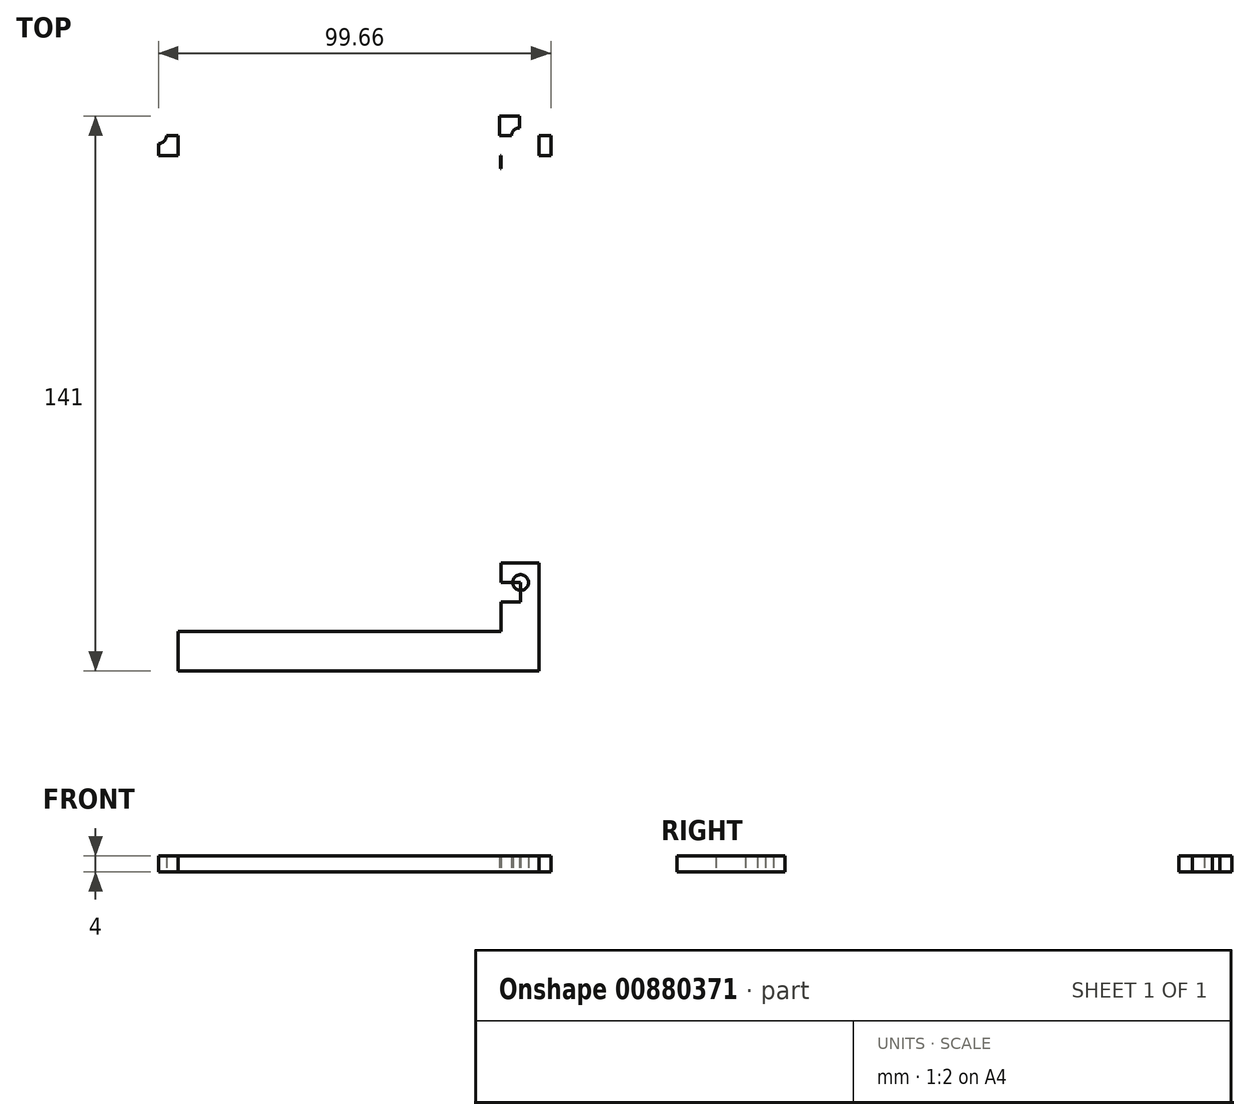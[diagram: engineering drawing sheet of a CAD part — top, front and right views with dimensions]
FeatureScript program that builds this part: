
annotation { "Feature Type Name" : "Feature", "Feature Type Description" : "" }
export const myFeature = defineFeature(function(context is Context, id is Id, definition is map)
    precondition{}
    {
        {
            var Q0;
            Q0=qCreatedBy(makeId("Top.planeOp"),FACE);
            var sketch = newSketch(context, id + "F0", { "sketchPlane" : qUnion([Q0])});
            skLineSegment(sketch, "E0.bottom", {"start": v(-139.68, -1.26) * mm, "end": v(-129.68, -1.26) * mm});
            skLineSegment(sketch, "E0.top", {"start": v(-139.68, -11.26) * mm, "end": v(-129.68, -11.26) * mm});
            skLineSegment(sketch, "E0.left", {"start": v(-139.68, -1.26) * mm, "end": v(-139.68, -11.26) * mm});
            skLineSegment(sketch, "E0.right", {"start": v(-129.68, -1.26) * mm, "end": v(-129.68, -11.26) * mm});
            skLineSegment(sketch, "E1.left", {"start": v(-129.68, -11.26) * mm, "end": v(-129.68, -114.76) * mm});
            skLineSegment(sketch, "E2.bottom", {"start": v(-124.68, -124.58) * mm, "end": v(-98.18, -124.58) * mm});
            skLineSegment(sketch, "E2.top", {"start": v(-124.68, -88.58) * mm, "end": v(-98.18, -88.58) * mm});
            skLineSegment(sketch, "E2.left", {"start": v(-124.68, -124.58) * mm, "end": v(-124.68, -88.58) * mm});
            skLineSegment(sketch, "E2.right", {"start": v(-98.18, -124.58) * mm, "end": v(-98.18, -88.58) * mm});
            skLineSegment(sketch, "E3.bottom", {"start": v(-129.68, -114.76) * mm, "end": v(-139.34, -114.76) * mm});
            skLineSegment(sketch, "E3.top", {"start": v(-129.68, -124.76) * mm, "end": v(-139.34, -124.76) * mm});
            skLineSegment(sketch, "E3.left", {"start": v(-129.68, -114.76) * mm, "end": v(-129.68, -124.76) * mm});
            skLineSegment(sketch, "E3.right", {"start": v(-139.34, -114.76) * mm, "end": v(-139.34, -124.76) * mm});
            skLineSegment(sketch, "E4", {"start": v(-129.68, -11.26) * mm, "end": v(-126.34, -11.26) * mm});
            skLineSegment(sketch, "E5.bottom", {"start": v(-129.68, -11.26) * mm, "end": v(-126.88, -11.26) * mm});
            skLineSegment(sketch, "E5.left", {"start": v(-129.68, -11.26) * mm, "end": v(-129.68, -14.06) * mm});
            skLineSegment(sketch, "E6.left", {"start": v(-129.68, -114.76) * mm, "end": v(-129.68, -111.76) * mm});
            skLineSegment(sketch, "E7.bottom", {"start": v(-98.18, -88.58) * mm, "end": v(-99.88, -88.58) * mm});
            skLineSegment(sketch, "E7.top", {"start": v(-98.18, -90.28) * mm, "end": v(-99.88, -90.28) * mm});
            skLineSegment(sketch, "E7.left", {"start": v(-98.18, -88.58) * mm, "end": v(-98.18, -90.28) * mm});
            skLineSegment(sketch, "E7.right", {"start": v(-99.88, -88.58) * mm, "end": v(-99.88, -90.28) * mm});
            skLineSegment(sketch, "E8.bottom", {"start": v(-124.68, -88.58) * mm, "end": v(-122.98, -88.58) * mm});
            skLineSegment(sketch, "E8.top", {"start": v(-124.68, -90.28) * mm, "end": v(-122.98, -90.28) * mm});
            skLineSegment(sketch, "E8.left", {"start": v(-124.68, -88.58) * mm, "end": v(-124.68, -90.28) * mm});
            skLineSegment(sketch, "E8.right", {"start": v(-122.98, -88.58) * mm, "end": v(-122.98, -90.28) * mm});
            skCircle(sketch, "E9", {"center": v(-122.98, -90.28) * mm, "radius": 1.2 * mm});
            skCircle(sketch, "E10", {"center": v(-99.88, -90.28) * mm, "radius": 1.2 * mm});
            skLineSegment(sketch, "E11.bottom", {"start": v(-139.34, -124.76) * mm, "end": v(-134.34, -124.76) * mm});
            skLineSegment(sketch, "E11.top", {"start": v(-139.34, -119.76) * mm, "end": v(-134.34, -119.76) * mm});
            skLineSegment(sketch, "E11.left", {"start": v(-139.34, -124.76) * mm, "end": v(-139.34, -119.76) * mm});
            skLineSegment(sketch, "E11.right", {"start": v(-134.34, -124.76) * mm, "end": v(-134.34, -119.76) * mm});
            skCircle(sketch, "E12", {"center": v(-134.34, -119.76) * mm, "radius": 2 * mm});
            skLineSegment(sketch, "E13.bottom", {"start": v(-139.68, -1.26) * mm, "end": v(-134.68, -1.26) * mm});
            skLineSegment(sketch, "E13.top", {"start": v(-139.68, -6.26) * mm, "end": v(-134.68, -6.26) * mm});
            skLineSegment(sketch, "E13.left", {"start": v(-139.68, -1.26) * mm, "end": v(-139.68, -6.26) * mm});
            skLineSegment(sketch, "E13.right", {"start": v(-134.68, -1.26) * mm, "end": v(-134.68, -6.26) * mm});
            skCircle(sketch, "E14", {"center": v(-134.68, -6.26) * mm, "radius": 2 * mm});
            skLineSegment(sketch, "E15.bottom", {"start": v(-129.68, -11.26) * mm, "end": v(-126.68, -11.26) * mm});
            skLineSegment(sketch, "E15.left", {"start": v(-129.68, -11.26) * mm, "end": v(-129.68, -27.96) * mm});
            skLineSegment(sketch, "E16.left", {"start": v(-129.68, -114.76) * mm, "end": v(-129.68, -108.76) * mm});
            skLineSegment(sketch, "E17.left", {"start": v(-129.68, -114.76) * mm, "end": v(-129.68, -27.46) * mm});
            skLineSegment(sketch, "E18.MirrorCS", {"start": v(-139.5, -132.26) * mm, "end": v(-139.5, -11.26) * mm});
            skLineSegment(sketch, "E19.MirrorCS", {"start": v(-221.34, -11.26) * mm, "end": v(-139.34, -11.26) * mm});
            skLineSegment(sketch, "E20.MirrorCS", {"start": v(-221.34, -132.26) * mm, "end": v(-139.34, -132.26) * mm});
            skCircle(sketch, "E21.MirrorC", {"center": v(-142.74, -128.86) * mm, "radius": 1.4 * mm});
            skCircle(sketch, "E22.MirrorC", {"center": v(-217.94, -128.86) * mm, "radius": 1.7 * mm});
            skCircle(sketch, "E23.MirrorC", {"center": v(-217.94, -14.66) * mm, "radius": 1.4 * mm});
            skCircle(sketch, "E24.MirrorC", {"center": v(-142.74, -14.66) * mm, "radius": 1.4 * mm});
            skLineSegment(sketch, "E25.MirrorCS", {"start": v(-142.74, -11.26) * mm, "end": v(-142.74, -14.66) * mm});
            skLineSegment(sketch, "E26.MirrorCS", {"start": v(-139.34, -14.66) * mm, "end": v(-142.74, -14.66) * mm});
            skLineSegment(sketch, "E27.MirrorCS", {"start": v(-217.94, -11.26) * mm, "end": v(-217.94, -14.66) * mm});
            skLineSegment(sketch, "E28.MirrorCS", {"start": v(-221.34, -14.66) * mm, "end": v(-217.94, -14.66) * mm});
            skLineSegment(sketch, "E29.MirrorCS", {"start": v(-142.74, -132.26) * mm, "end": v(-142.74, -128.86) * mm});
            skLineSegment(sketch, "E30.MirrorCS", {"start": v(-139.34, -128.86) * mm, "end": v(-142.74, -128.86) * mm});
            skLineSegment(sketch, "E31.MirrorCS", {"start": v(-221.34, -128.86) * mm, "end": v(-217.94, -128.86) * mm});
            skLineSegment(sketch, "E32.MirrorCS", {"start": v(-217.94, -132.26) * mm, "end": v(-217.94, -128.86) * mm});
            skLineSegment(sketch, "E33", {"start": v(-221.34, -11.26) * mm, "end": v(-221.34, -1.26) * mm});
            skLineSegment(sketch, "E34", {"start": v(-221.34, -132.26) * mm, "end": v(-221.34, -11.26) * mm});
            skLineSegment(sketch, "E35", {"start": v(-221.34, -132.26) * mm, "end": v(-231.5, -132.26) * mm});
            skLineSegment(sketch, "E36.bottom", {"start": v(-221.34, -132.26) * mm, "end": v(-231.34, -132.26) * mm});
            skLineSegment(sketch, "E36.top", {"start": v(-221.34, -142.26) * mm, "end": v(-231.34, -142.26) * mm});
            skLineSegment(sketch, "E36.left", {"start": v(-221.34, -132.26) * mm, "end": v(-221.34, -142.26) * mm});
            skLineSegment(sketch, "E36.right", {"start": v(-231.34, -132.26) * mm, "end": v(-231.34, -142.26) * mm});
            skLineSegment(sketch, "E37.bottom", {"start": v(-221.34, -142.26) * mm, "end": v(-139.34, -142.26) * mm});
            skLineSegment(sketch, "E37.left", {"start": v(-221.34, -142.26) * mm, "end": v(-221.34, -132.26) * mm});
            skLineSegment(sketch, "E38", {"start": v(-231.34, -132.26) * mm, "end": v(-231.34, -1.26) * mm});
            skLineSegment(sketch, "E39.bottom", {"start": v(-129.68, -124.76) * mm, "end": v(-139.53, -124.76) * mm});
            skLineSegment(sketch, "E39.top", {"start": v(-129.68, -142.26) * mm, "end": v(-139.34, -142.26) * mm});
            skLineSegment(sketch, "E39.left", {"start": v(-129.68, -124.76) * mm, "end": v(-129.68, -142.26) * mm});
            skLineSegment(sketch, "E40", {"start": v(-139.34, -142.26) * mm, "end": v(-139.5, -132.26) * mm});
            skLineSegment(sketch, "E41.bottom", {"start": v(-231.34, -142.26) * mm, "end": v(-226.34, -142.26) * mm});
            skLineSegment(sketch, "E41.top", {"start": v(-231.34, -137.4) * mm, "end": v(-226.34, -137.4) * mm});
            skLineSegment(sketch, "E41.left", {"start": v(-231.34, -142.26) * mm, "end": v(-231.34, -137.4) * mm});
            skLineSegment(sketch, "E41.right", {"start": v(-226.34, -142.26) * mm, "end": v(-226.34, -137.4) * mm});
            skCircle(sketch, "E42", {"center": v(-226.34, -137.4) * mm, "radius": 2 * mm});
            skLineSegment(sketch, "E43.bottom", {"start": v(-221.34, -11.26) * mm, "end": v(-226.34, -11.26) * mm});
            skLineSegment(sketch, "E43.top", {"start": v(-221.34, -6.26) * mm, "end": v(-226.34, -6.26) * mm});
            skLineSegment(sketch, "E43.left", {"start": v(-221.34, -11.26) * mm, "end": v(-221.34, -6.26) * mm});
            skLineSegment(sketch, "E43.right", {"start": v(-226.34, -11.26) * mm, "end": v(-226.34, -6.26) * mm});
            skCircle(sketch, "E44", {"center": v(-226.34, -6.26) * mm, "radius": 2 * mm});
            skLineSegment(sketch, "E45.bottom", {"start": v(-129.68, -142.26) * mm, "end": v(-87.68, -142.26) * mm});
            skLineSegment(sketch, "E45.left", {"start": v(-129.68, -142.26) * mm, "end": v(-129.68, -114.76) * mm});
            skLineSegment(sketch, "E46.bottom", {"start": v(-139.34, -132.26) * mm, "end": v(-151.42, -132.26) * mm});
            skLineSegment(sketch, "E46.top", {"start": v(-139.34, -11.26) * mm, "end": v(-151.42, -11.26) * mm});
            skLineSegment(sketch, "E46.left", {"start": v(-139.34, -132.26) * mm, "end": v(-139.34, -11.26) * mm});
            skLineSegment(sketch, "E47.bottom", {"start": v(-151.42, -132.26) * mm, "end": v(-147.42, -132.26) * mm});
            skLineSegment(sketch, "E47.top", {"start": v(-151.42, -11.26) * mm, "end": v(-147.42, -11.26) * mm});
            skLineSegment(sketch, "E48.bottom", {"start": v(-129.68, -11.26) * mm, "end": v(-97.68, -11.26) * mm});
            skLineSegment(sketch, "E48.top", {"start": v(-129.68, -78.26) * mm, "end": v(-97.68, -78.26) * mm});
            skLineSegment(sketch, "E48.left", {"start": v(-129.68, -11.26) * mm, "end": v(-129.68, -78.26) * mm});
            skLineSegment(sketch, "E48.right", {"start": v(-97.68, -11.26) * mm, "end": v(-97.68, -78.26) * mm});
            skLineSegment(sketch, "E49.bottom", {"start": v(-129.68, -78.26) * mm, "end": v(-126.34, -78.26) * mm});
            skLineSegment(sketch, "E49.left", {"start": v(-129.68, -78.26) * mm, "end": v(-129.68, -74.92) * mm});
            skLineSegment(sketch, "E50.bottom", {"start": v(-97.68, -78.26) * mm, "end": v(-101.02, -78.26) * mm});
            skLineSegment(sketch, "E50.left", {"start": v(-97.68, -78.26) * mm, "end": v(-97.68, -74.92) * mm});
            skLineSegment(sketch, "E51.left", {"start": v(-129.68, -11.26) * mm, "end": v(-129.68, -14.6) * mm});
            skLineSegment(sketch, "E52.bottom", {"start": v(-97.68, -11.26) * mm, "end": v(-101.02, -11.26) * mm});
            skLineSegment(sketch, "E52.left", {"start": v(-97.68, -11.26) * mm, "end": v(-97.68, -14.6) * mm});
            skCircle(sketch, "E53", {"center": v(-126.34, -74.92) * mm, "radius": 1.5 * mm});
            skCircle(sketch, "E54", {"center": v(-100.68, -74.92) * mm, "radius": 1.5 * mm});
            skCircle(sketch, "E55", {"center": v(-100.68, -14.6) * mm, "radius": 1.5 * mm});
            skCircle(sketch, "E56", {"center": v(-126, -14.6) * mm, "radius": 1.5 * mm});
            skLineSegment(sketch, "E57", {"start": v(-231.34, -1.26) * mm, "end": v(-139.68, -1.26) * mm});
            skLineSegment(sketch, "E58", {"start": v(-87.68, -1.26) * mm, "end": v(-87.68, -142.26) * mm});
            skLineSegment(sketch, "E59.bottom", {"start": v(-129.68, -11.26) * mm, "end": v(-97.34, -11.26) * mm});
            skLineSegment(sketch, "E59.top", {"start": v(-129.68, -6.26) * mm, "end": v(-97.34, -6.26) * mm});
            skLineSegment(sketch, "E59.left", {"start": v(-129.68, -11.26) * mm, "end": v(-129.68, -6.26) * mm});
            skLineSegment(sketch, "E60", {"start": v(-87.68, -1.26) * mm, "end": v(-129.68, -1.26) * mm});
            skLineSegment(sketch, "E61.top", {"start": v(-129.68, -6.26) * mm, "end": v(-126.68, -6.26) * mm});
            skLineSegment(sketch, "E61.right", {"start": v(-126.68, -11.26) * mm, "end": v(-126.68, -6.26) * mm});
            skLineSegment(sketch, "E62.right", {"start": v(-97.68, -11.26) * mm, "end": v(-97.68, -11.26) * mm});
            skLineSegment(sketch, "E63.bottom", {"start": v(-97.68, -11.26) * mm, "end": v(-100.68, -11.26) * mm});
            skLineSegment(sketch, "E63.top", {"start": v(-97.68, -6.26) * mm, "end": v(-100.68, -6.26) * mm});
            skLineSegment(sketch, "E63.left", {"start": v(-97.68, -11.26) * mm, "end": v(-97.68, -6.26) * mm});
            skLineSegment(sketch, "E63.right", {"start": v(-100.68, -11.26) * mm, "end": v(-100.68, -6.26) * mm});
            skLineSegment(sketch, "E64.bottom", {"start": v(-87.68, -142.26) * mm, "end": v(-92.68, -142.26) * mm});
            skLineSegment(sketch, "E64.top", {"start": v(-87.68, -137.26) * mm, "end": v(-92.68, -137.26) * mm});
            skLineSegment(sketch, "E64.left", {"start": v(-87.68, -142.26) * mm, "end": v(-87.68, -137.26) * mm});
            skLineSegment(sketch, "E64.right", {"start": v(-92.68, -142.26) * mm, "end": v(-92.68, -137.26) * mm});
            skLineSegment(sketch, "E65.bottom", {"start": v(-87.68, -1.26) * mm, "end": v(-92.68, -1.26) * mm});
            skLineSegment(sketch, "E65.top", {"start": v(-87.68, -6.26) * mm, "end": v(-92.68, -6.26) * mm});
            skLineSegment(sketch, "E65.left", {"start": v(-87.68, -1.26) * mm, "end": v(-87.68, -6.26) * mm});
            skLineSegment(sketch, "E65.right", {"start": v(-92.68, -1.26) * mm, "end": v(-92.68, -6.26) * mm});
            skCircle(sketch, "E66", {"center": v(-92.68, -137.26) * mm, "radius": 2 * mm});
            skCircle(sketch, "E67", {"center": v(-92.68, -6.26) * mm, "radius": 2 * mm});
            skLineSegment(sketch, "E68.bottom", {"start": v(-221.34, -11.26) * mm, "end": v(-216.34, -11.26) * mm});
            skLineSegment(sketch, "E68.top", {"start": v(-221.34, -1.26) * mm, "end": v(-216.34, -1.26) * mm});
            skLineSegment(sketch, "E68.right", {"start": v(-216.34, -11.26) * mm, "end": v(-216.34, -1.26) * mm});
            skLineSegment(sketch, "E69.bottom", {"start": v(-139.68, -11.26) * mm, "end": v(-144.68, -11.26) * mm});
            skLineSegment(sketch, "E69.top", {"start": v(-139.68, -1.26) * mm, "end": v(-144.68, -1.26) * mm});
            skLineSegment(sketch, "E69.left", {"start": v(-139.68, -11.26) * mm, "end": v(-139.68, -1.26) * mm});
            skLineSegment(sketch, "E69.right", {"start": v(-144.68, -11.26) * mm, "end": v(-144.68, -1.26) * mm});
            skSolve(sketch);
        }
        {
            var Q0;
            {var subQ1=sQuery(id+"F0.wireOp",EDGE,"E41.bottom");Q0=makeQuery(id+"F0.imprint","IMPRINT",FACE,{"disambiguationData":[TD([[makeQuery(id+"F0.imprint","IMPRINT",EDGE,{"derivedFrom":subQ1}),1.0]])]});}
            var Q1;
            {var subQ1=sQuery(id+"F0.wireOp",EDGE,"E64.bottom");Q1=makeQuery(id+"F0.imprint","IMPRINT",FACE,{"disambiguationData":[TD([[makeQuery(id+"F0.imprint","IMPRINT",EDGE,{"derivedFrom":subQ1}),-1.0]])]});}
            var Q2;
            {var subQ1=sQuery(id+"F0.wireOp",EDGE,"E65.bottom");Q2=makeQuery(id+"F0.imprint","IMPRINT",FACE,{"disambiguationData":[TD([[makeQuery(id+"F0.imprint","IMPRINT",EDGE,{"derivedFrom":subQ1}),1.0]])]});}
            var Q3;
            {var subQ1=sQuery(id+"F0.wireOp",EDGE,"E13.bottom");Q3=makeQuery(id+"F0.imprint","IMPRINT",FACE,{"disambiguationData":[TD([[makeQuery(id+"F0.imprint","IMPRINT",EDGE,{"derivedFrom":subQ1}),-1.0]])]});}
            var Q4;
            Q4=makeQuery(id+"F0.imprint","IMPRINT",FACE,{"disambiguationData":[TD([[makeQuery(id+"F0.imprint","IMPRINT",EDGE,{"derivedFrom":sQuery(id+"F0.wireOp",EDGE,"E36.bottom")}),1.0]])]});
            var Q5;
            Q5=makeQuery(id+"F0.imprint","IMPRINT",FACE,{"disambiguationData":[TD([[makeQuery(id+"F0.imprint","IMPRINT",EDGE,{"derivedFrom":sQuery(id+"F0.wireOp",EDGE,"E37.bottom")}),1.0]])]});
            var Q6;
            {var subQ4=sQuery(id+"F0.wireOp",EDGE,"E68.top");Q6=makeQuery(id+"F0.imprint","IMPRINT",FACE,{"disambiguationData":[TD([[makeQuery(id+"F0.imprint","IMPRINT",EDGE,{"derivedFrom":subQ4}),-1.0]])]});}
            var Q7;
            {var subQ5=sQuery(id+"F0.wireOp",EDGE,"E69.top");Q7=makeQuery(id+"F0.imprint","IMPRINT",FACE,{"disambiguationData":[TD([[makeQuery(id+"F0.imprint","IMPRINT",EDGE,{"derivedFrom":subQ5}),1.0]])]});}
            var Q8;
            {var subQ1=sQuery(id+"F0.wireOp",EDGE,"E39.top");Q8=makeQuery(id+"F0.imprint","IMPRINT",FACE,{"disambiguationData":[TD([[makeQuery(id+"F0.imprint","IMPRINT",EDGE,{"derivedFrom":subQ1}),-1.0]])]});}
            var Q9;
            {var subQ12=sQuery(id+"F0.wireOp",EDGE,"E36.bottom");Q9=makeQuery(id+"F0.imprint","IMPRINT",FACE,{"disambiguationData":[TD([[makeQuery(id+"F0.imprint","IMPRINT",EDGE,{"derivedFrom":subQ12}),-1.0]])]});}
            var Q10;
            {var subQ8=sQuery(id+"F0.wireOp",EDGE,"E0.bottom");Q10=makeQuery(id+"F0.imprint","IMPRINT",FACE,{"disambiguationData":[TD([[makeQuery(id+"F0.imprint","IMPRINT",EDGE,{"derivedFrom":subQ8}),-1.0]])]});}
            var Q11;
            Q11=makeQuery(id+"F0.imprint","IMPRINT",FACE,{"disambiguationData":[TD([[makeQuery(id+"F0.imprint","IMPRINT",EDGE,{"derivedFrom":sQuery(id+"F0.wireOp",EDGE,"E0.right")}),1.0]])]});
            var Q12;
            {var subQ6=sQuery(id+"F0.wireOp",EDGE,"E0.top");Q12=makeQuery(id+"F0.imprint","IMPRINT",FACE,{"disambiguationData":[TD([[makeQuery(id+"F0.imprint","IMPRINT",EDGE,{"derivedFrom":subQ6}),-1.0]])]});}
            var Q13;
            {var subQ3=sQuery(id+"F0.wireOp",EDGE,"E46.left");var subQ6=sQuery(id+"F0.wireOp",EDGE,"E11.top");var subQ9=makeQuery(id+"F0.imprint","INTERSECT",VERTEX,{"derivedFrom":[subQ6,subQ3]});Q13=makeQuery(id+"F0.imprint","IMPRINT",FACE,{"disambiguationData":[TD([[makeQuery(id+"F0.imprint","IMPRINT",EDGE,{"disambiguationData":[TD([[subQ9,-1.0]])],"derivedFrom":subQ6}),-1.0]])]});}
            var Q14;
            {var subQ6=sQuery(id+"F0.wireOp",EDGE,"E3.bottom");Q14=makeQuery(id+"F0.imprint","IMPRINT",FACE,{"disambiguationData":[TD([[makeQuery(id+"F0.imprint","IMPRINT",EDGE,{"derivedFrom":subQ6}),1.0]])]});}
            var Q15;
            {var subQ1=sQuery(id+"F0.wireOp",EDGE,"E43.bottom");Q15=makeQuery(id+"F0.imprint","IMPRINT",FACE,{"disambiguationData":[TD([[makeQuery(id+"F0.imprint","IMPRINT",EDGE,{"derivedFrom":subQ1}),-1.0]])]});}
            var Q16;
            Q16=makeQuery(id+"F0.imprint","IMPRINT",FACE,{"disambiguationData":[TD([[makeQuery(id+"F0.imprint","IMPRINT",EDGE,{"derivedFrom":sQuery(id+"F0.wireOp",EDGE,"E61.top")}),-1.0]])]});
            var Q17;
            Q17=makeQuery(id+"F0.imprint","IMPRINT",FACE,{"disambiguationData":[TD([[makeQuery(id+"F0.imprint","IMPRINT",EDGE,{"derivedFrom":sQuery(id+"F0.wireOp",EDGE,"E63.bottom")}),-1.0]])]});
            extrude(context, id + "F1", {"entities" : qUnion([Q0, Q1, Q2, Q3, Q4, Q5, Q6, Q7, Q8, Q9, Q10, Q11, Q12, Q13, Q14, Q15, Q16, Q17]), "depth" : 4 * mm, "offsetDistance" : 25 * mm});
        }
    });
